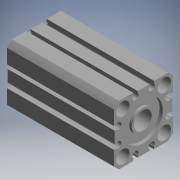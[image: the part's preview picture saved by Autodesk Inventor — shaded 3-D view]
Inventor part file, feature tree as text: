
AUTODESK INVENTOR PART (.ipt)
format: ipt  version: 2017.3 (Build 213256000, 256)  size: 273,920 bytes
history: native  units: mm (DEFAULTED — no unit token found)
features: sketch x7, revolve x4, thread x4, extrude x3, pattern_linear x1
ambient origin geometry x8: Origin, YZ Plane, XZ Plane, XY Plane, X Axis, Y Axis, Z Axis, Center Point
bodies: Solid1 (feature_tree), BODY_DUMMY_XY (feature_tree), BODY_DUMMY_YZ (feature_tree), BODY_DUMMY_ZX (feature_tree), BODY_DUMMY_X (feature_tree), BODY_DUMMY_Y (feature_tree), BODY_DUMMY_Z (feature_tree), BODY_DUMMY_Center (feature_tree), BODY_MOUBT1_XY (feature_tree), BODY_MOUBT1_YZ (feature_tree), BODY_MOUBT1_ZX (feature_tree), BODY_MOUBT1_X (feature_tree), BODY_MOUBT1_Y (feature_tree), BODY_MOUBT1_Z (feature_tree), BODY_MOUBT1_Center (feature_tree), BODY_MOUBT2_XY (feature_tree), BODY_MOUBT2_YZ (feature_tree), BODY_MOUBT2_ZX (feature_tree), BODY_MOUBT2_X (feature_tree), BODY_MOUBT2_Y (feature_tree), BODY_MOUBT2_Z (feature_tree), BODY_MOUBT2_Center (feature_tree), BODY_ROD_XY (feature_tree), BODY_ROD_YZ (feature_tree), BODY_ROD_ZX (feature_tree), BODY_ROD_X (feature_tree), BODY_ROD_Y (feature_tree), BODY_ROD_Z (feature_tree), BODY_ROD_Center (feature_tree), BODY_SWA_XY (feature_tree), BODY_SWA_YZ (feature_tree), BODY_SWA_ZX (feature_tree), BODY_SWA_X (feature_tree), BODY_SWA_Y (feature_tree), BODY_SWA_Z (feature_tree), BODY_SWA_Center (feature_tree), BODY_SWB_XY (feature_tree), BODY_SWB_YZ (feature_tree), BODY_SWB_ZX (feature_tree), BODY_SWB_X (feature_tree), BODY_SWB_Y (feature_tree), BODY_SWB_Z (feature_tree), BODY_SWB_Center (feature_tree)
feature tree (19):
  extrude  "Extrusion1"  TaperAngle=360.0deg  [1 undecoded]
  revolve  "Revolution1"  [1 undecoded]
  thread  "Thread1"  [1 undecoded]
  thread  "Thread2"  [1 undecoded]
  pattern_linear  "Rectangular Pattern1"  Spacing1=0.5mm  [1 undecoded]
  revolve  "Revolution2"  [1 undecoded]
  revolve  "Revolution3"  [1 undecoded]
  thread  "Thread3"  [1 undecoded]
  revolve  "Revolution4"  [1 undecoded]
  thread  "Thread4"  [1 undecoded]
  extrude  "Extrusion2"  [1 undecoded]
  extrude  "Extrusion3"  [1 undecoded]
  sketch  "Sketch_13"  dims[d17=360.0deg]
  sketch  "Sketch_2"  dims[d0=72.5mm d1=0.0mm d2=360.0deg]
  sketch  "Sketch_5"  dims[d14=360.0deg]
  sketch  "Sketch_4"  dims[d3=9.4585mm d4=0.0mm d5=9.4585mm d6=0.0mm d7=20.0mm d9=28.0mm d10=20.0mm d12=28.0mm d13=360.0deg]
  sketch  "Sketch_6"  dims[d15=4.567mm d16=0.0mm]
  sketch  "Sketch_26"  dims[d18=4.567mm d19=0.0mm]
  sketch  "Sketch_27"  dims[d20=2.15mm d21=0.0mm d22=0.5mm d23=0.0mm d24=0.0mm d25=0.0mm d26=0.0mm d27=0.0mm]
note: 12 required parameter values undecoded (feature->parameter linkage not recoverable at this tier; creation-order binding heuristic only, values carry confidence <= 0.55)